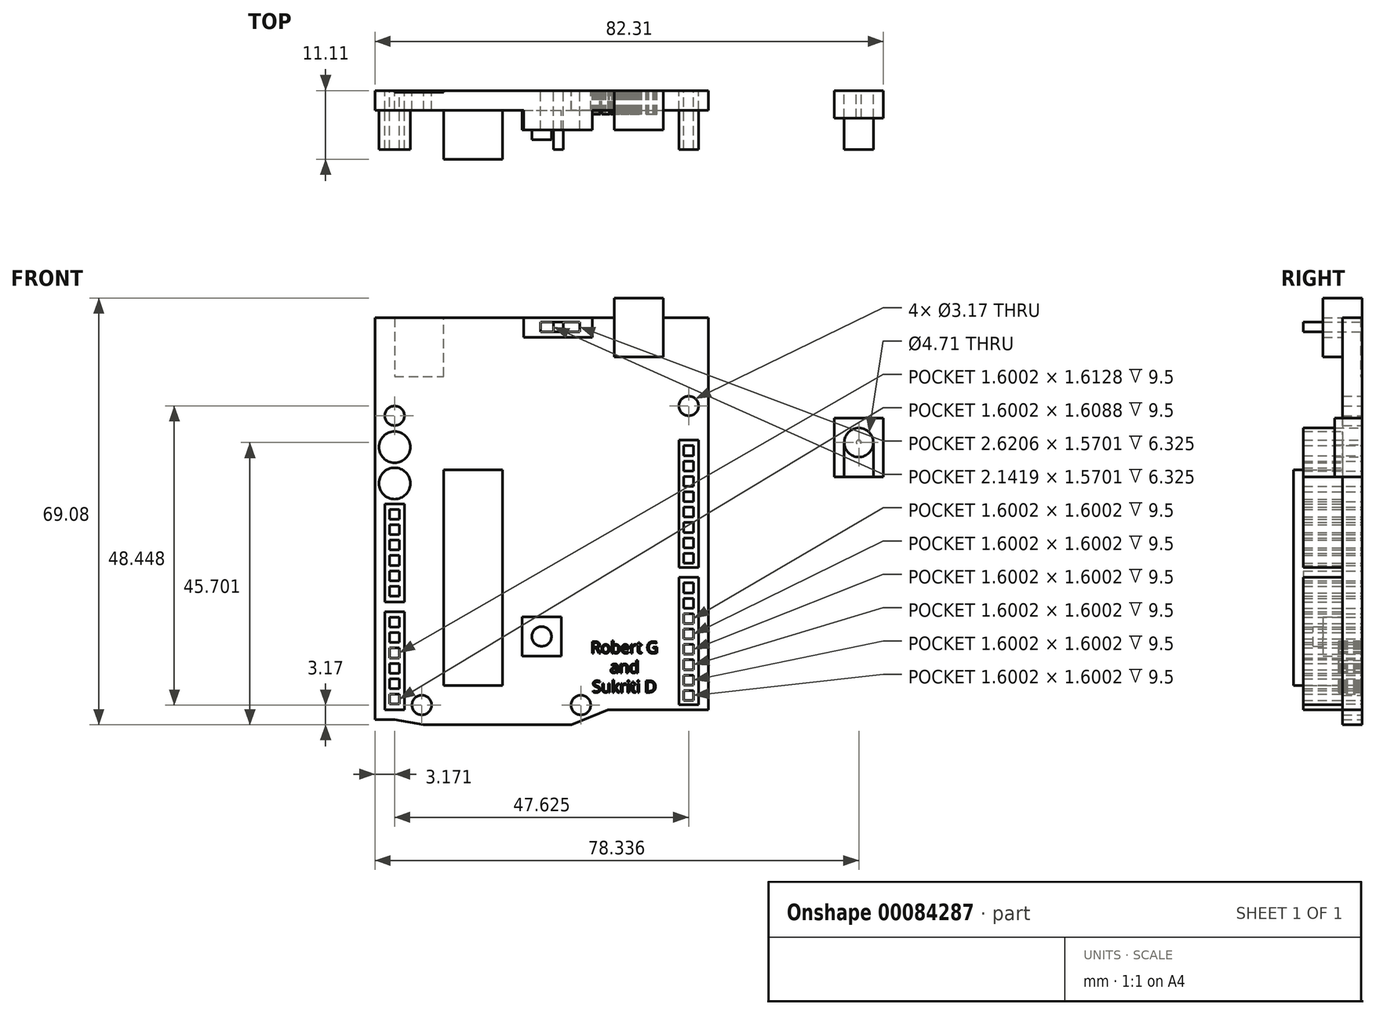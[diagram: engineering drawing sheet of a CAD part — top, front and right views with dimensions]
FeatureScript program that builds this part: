
annotation { "Feature Type Name" : "Feature", "Feature Type Description" : "" }
export const myFeature = defineFeature(function(context is Context, id is Id, definition is map)
    precondition{}
    {
        {
            var Q0;
            Q0=qCreatedBy(makeId("Front.planeOp"),FACE);
            var sketch = newSketch(context, id + "F0", { "sketchPlane" : qUnion([Q0])});
            skLineSegment(sketch, "E0.bottom", {"start": v(-35.3, 35.34) * mm, "end": v(18.68, 35.34) * mm});
            skLineSegment(sketch, "E0.top", {"start": v(-27.43, -30.57) * mm, "end": v(-3.44, -30.57) * mm});
            skLineSegment(sketch, "E0.left", {"start": v(-35.3, 35.34) * mm, "end": v(-35.3, -29.75) * mm});
            skLineSegment(sketch, "E0.right", {"start": v(18.68, 35.34) * mm, "end": v(18.68, -28.16) * mm});
            skLineSegment(sketch, "E1.bottom", {"start": v(-35.3, -29.75) * mm, "end": v(-32.12, -29.75) * mm});
            skPoint(sketch, "E2", {"position": v(-3.44, -30.57) * mm});
            skPoint(sketch, "E3.orphan", {"position": v(18.68, -30.57) * mm});
            skLineSegment(sketch, "E4", {"start": v(-32.12, -29.75) * mm, "end": v(-27.43, -30.57) * mm});
            skPoint(sketch, "E1.right.end.orphan", {"position": v(-35.19, -30.57) * mm});
            skLineSegment(sketch, "E5", {"start": v(-3.44, -30.57) * mm, "end": v(0.98, -28.76) * mm});
            skLineSegment(sketch, "E6", {"start": v(2.42, -28.16) * mm, "end": v(18.68, -28.16) * mm});
            skPoint(sketch, "E7.orphan", {"position": v(18.68, -30.95) * mm});
            skLineSegment(sketch, "E8", {"start": v(0.98, -28.76) * mm, "end": v(2.42, -28.16) * mm});
            skCircle(sketch, "E9", {"center": v(-27.72, -27.39) * mm, "radius": 1.59 * mm});
            skCircle(sketch, "E10", {"center": v(-1.96, -27.4) * mm, "radius": 1.59 * mm});
            skCircle(sketch, "E11", {"center": v(-32.12, 19.46) * mm, "radius": 1.59 * mm});
            skCircle(sketch, "E12", {"center": v(15.5, 21.05) * mm, "radius": 1.59 * mm});
            skLineSegment(sketch, "E13.bottom", {"start": v(11.14, 38.51) * mm, "end": v(11.4, 38.51) * mm});
            skLineSegment(sketch, "E13.top", {"start": v(3.47, 28.99) * mm, "end": v(11.4, 28.99) * mm});
            skLineSegment(sketch, "E14.bottom", {"start": v(13.92, -6.73) * mm, "end": v(17.1, -6.73) * mm});
            skLineSegment(sketch, "E14.top", {"start": v(13.92, -27.37) * mm, "end": v(17.1, -27.37) * mm});
            skLineSegment(sketch, "E14.left", {"start": v(13.92, -6.73) * mm, "end": v(13.92, -27.37) * mm});
            skLineSegment(sketch, "E14.right", {"start": v(17.1, -6.73) * mm, "end": v(17.1, -27.37) * mm});
            skLineSegment(sketch, "E15.bottom", {"start": v(13.92, 15.5) * mm, "end": v(17.1, 15.5) * mm});
            skLineSegment(sketch, "E15.top", {"start": v(13.92, -5.14) * mm, "end": v(17.1, -5.14) * mm});
            skLineSegment(sketch, "E15.left", {"start": v(13.92, 15.5) * mm, "end": v(13.92, -5.14) * mm});
            skLineSegment(sketch, "E15.right", {"start": v(17.1, 15.5) * mm, "end": v(17.1, -5.14) * mm});
            skLineSegment(sketch, "E16.bottom", {"start": v(-33.7, -12.29) * mm, "end": v(-30.53, -12.29) * mm});
            skLineSegment(sketch, "E16.top", {"start": v(-33.7, -28.16) * mm, "end": v(-30.53, -28.16) * mm});
            skLineSegment(sketch, "E16.left", {"start": v(-33.7, -12.29) * mm, "end": v(-33.7, -28.16) * mm});
            skLineSegment(sketch, "E16.right", {"start": v(-30.53, -12.29) * mm, "end": v(-30.53, -28.16) * mm});
            skLineSegment(sketch, "E17", {"start": v(-3.44, -30.57) * mm, "end": v(2.42, -28.16) * mm});
            skLineSegment(sketch, "E18.bottom", {"start": v(-33.7, 5.17) * mm, "end": v(-30.53, 5.17) * mm});
            skLineSegment(sketch, "E18.top", {"start": v(-33.7, -10.7) * mm, "end": v(-30.53, -10.7) * mm});
            skLineSegment(sketch, "E18.left", {"start": v(-33.7, 5.17) * mm, "end": v(-33.7, -10.7) * mm});
            skLineSegment(sketch, "E18.right", {"start": v(-30.53, 5.17) * mm, "end": v(-30.53, -10.7) * mm});
            skLineSegment(sketch, "E19.bottom", {"start": v(-24.18, -24.22) * mm, "end": v(-14.66, -24.22) * mm});
            skLineSegment(sketch, "E19.top", {"start": v(-24.18, 10.7) * mm, "end": v(-14.66, 10.7) * mm});
            skLineSegment(sketch, "E19.left", {"start": v(-24.18, -24.22) * mm, "end": v(-24.18, 10.7) * mm});
            skLineSegment(sketch, "E19.right", {"start": v(-14.66, -24.22) * mm, "end": v(-14.66, 10.7) * mm});
            skLineSegment(sketch, "E20.bottom", {"start": v(-11.48, -13.11) * mm, "end": v(-5.13, -13.11) * mm});
            skLineSegment(sketch, "E20.top", {"start": v(-11.48, -19.46) * mm, "end": v(-5.13, -19.46) * mm});
            skLineSegment(sketch, "E20.left", {"start": v(-11.48, -13.11) * mm, "end": v(-11.48, -19.46) * mm});
            skLineSegment(sketch, "E20.right", {"start": v(-5.13, -13.11) * mm, "end": v(-5.13, -19.46) * mm});
            skCircle(sketch, "E21", {"center": v(-8.3, -16.29) * mm, "radius": 1.59 * mm});
            skLineSegment(sketch, "E22.bottom", {"start": v(-11.2, 32.16) * mm, "end": v(-0.08, 32.16) * mm});
            skLineSegment(sketch, "E22.top", {"start": v(-11.2, 35.34) * mm, "end": v(-0.08, 35.34) * mm});
            skLineSegment(sketch, "E22.left", {"start": v(-11.2, 32.16) * mm, "end": v(-11.2, 35.34) * mm});
            skLineSegment(sketch, "E22.right", {"start": v(-0.08, 32.16) * mm, "end": v(-0.08, 35.34) * mm});
            skLineSegment(sketch, "E23.bottom", {"start": v(-8.5, 33.07) * mm, "end": v(-2.16, 33.07) * mm});
            skLineSegment(sketch, "E23.top", {"start": v(-8.5, 34.64) * mm, "end": v(-2.16, 34.64) * mm});
            skLineSegment(sketch, "E23.left", {"start": v(-8.5, 33.07) * mm, "end": v(-8.5, 34.64) * mm});
            skLineSegment(sketch, "E24", {"start": v(-2.16, 34.64) * mm, "end": v(-2.16, 33.07) * mm});
            skLineSegment(sketch, "E25", {"start": v(-4.78, 34.64) * mm, "end": v(-4.78, 33.07) * mm});
            skLineSegment(sketch, "E26", {"start": v(-6.37, 34.64) * mm, "end": v(-6.37, 33.07) * mm});
            skLineSegment(sketch, "E27", {"start": v(11.4, 36.51) * mm, "end": v(11.4, 35.34) * mm});
            skLineSegment(sketch, "E28.trimOffspring", {"start": v(3.47, 35.34) * mm, "end": v(3.47, 28.99) * mm});
            skLineSegment(sketch, "E29.trimOffspring", {"start": v(11.4, 35.34) * mm, "end": v(11.4, 28.99) * mm});
            skPoint(sketch, "E30.orphan", {"position": v(3.47, 38.51) * mm});
            skLineSegment(sketch, "E31", {"start": v(3.47, 35.34) * mm, "end": v(3.47, 36.51) * mm});
            skLineSegment(sketch, "E32", {"start": v(11.14, 38.51) * mm, "end": v(3.73, 38.51) * mm});
            skLineSegment(sketch, "E33", {"start": v(-32.12, 35.34) * mm, "end": v(-32.12, 25.81) * mm});
            skLineSegment(sketch, "E34", {"start": v(-32.12, 25.81) * mm, "end": v(-24.17, 25.81) * mm});
            skLineSegment(sketch, "E35", {"start": v(-24.17, 25.81) * mm, "end": v(-24.17, 35.34) * mm});
            skLineSegment(sketch, "E36.bottom", {"start": v(-32.9, 4.28) * mm, "end": v(-31.32, 4.28) * mm});
            skLineSegment(sketch, "E36.top", {"start": v(-32.9, 2.7) * mm, "end": v(-31.32, 2.7) * mm});
            skLineSegment(sketch, "E36.left", {"start": v(-32.9, 4.28) * mm, "end": v(-32.9, 2.7) * mm});
            skLineSegment(sketch, "E36.right", {"start": v(-31.32, 4.28) * mm, "end": v(-31.32, 2.7) * mm});
            skLineSegment(sketch, "E37.left", {"start": v(-32.9, 1.25) * mm, "end": v(-32.9, 1.22) * mm});
            skLineSegment(sketch, "E37.right", {"start": v(-31.53, 1.25) * mm, "end": v(-31.53, 1.22) * mm});
            skLineSegment(sketch, "E38.bottom", {"start": v(-32.9, 1.8) * mm, "end": v(-31.32, 1.8) * mm});
            skLineSegment(sketch, "E38.top", {"start": v(-32.9, 0.2) * mm, "end": v(-31.32, 0.2) * mm});
            skLineSegment(sketch, "E38.left", {"start": v(-32.9, 1.8) * mm, "end": v(-32.9, 0.2) * mm});
            skLineSegment(sketch, "E38.right", {"start": v(-31.32, 1.8) * mm, "end": v(-31.32, 0.2) * mm});
            skLineSegment(sketch, "E39.bottom", {"start": v(-32.9, -0.68) * mm, "end": v(-31.32, -0.68) * mm});
            skLineSegment(sketch, "E39.top", {"start": v(-32.9, -2.28) * mm, "end": v(-31.32, -2.28) * mm});
            skLineSegment(sketch, "E39.left", {"start": v(-32.9, -0.68) * mm, "end": v(-32.9, -2.28) * mm});
            skLineSegment(sketch, "E39.right", {"start": v(-31.32, -0.68) * mm, "end": v(-31.32, -2.28) * mm});
            skLineSegment(sketch, "E40.bottom", {"start": v(-32.9, -3.17) * mm, "end": v(-31.32, -3.17) * mm});
            skLineSegment(sketch, "E40.top", {"start": v(-32.9, -4.77) * mm, "end": v(-31.32, -4.77) * mm});
            skLineSegment(sketch, "E40.left", {"start": v(-32.9, -3.17) * mm, "end": v(-32.9, -4.77) * mm});
            skLineSegment(sketch, "E40.right", {"start": v(-31.32, -3.17) * mm, "end": v(-31.32, -4.77) * mm});
            skLineSegment(sketch, "E41.bottom", {"start": v(-32.9, -5.66) * mm, "end": v(-31.32, -5.66) * mm});
            skLineSegment(sketch, "E41.top", {"start": v(-32.9, -7.26) * mm, "end": v(-31.32, -7.26) * mm});
            skLineSegment(sketch, "E41.left", {"start": v(-32.9, -5.66) * mm, "end": v(-32.9, -7.26) * mm});
            skLineSegment(sketch, "E41.right", {"start": v(-31.32, -5.66) * mm, "end": v(-31.32, -7.26) * mm});
            skLineSegment(sketch, "E42.bottom", {"start": v(-32.9, -8.15) * mm, "end": v(-31.32, -8.15) * mm});
            skLineSegment(sketch, "E42.top", {"start": v(-32.9, -9.75) * mm, "end": v(-31.32, -9.75) * mm});
            skLineSegment(sketch, "E42.left", {"start": v(-32.9, -8.15) * mm, "end": v(-32.9, -9.75) * mm});
            skLineSegment(sketch, "E42.right", {"start": v(-31.32, -8.15) * mm, "end": v(-31.32, -9.75) * mm});
            skLineSegment(sketch, "E43.bottom", {"start": v(-32.92, -13.18) * mm, "end": v(-31.32, -13.18) * mm});
            skLineSegment(sketch, "E43.top", {"start": v(-32.92, -14.78) * mm, "end": v(-31.32, -14.78) * mm});
            skLineSegment(sketch, "E43.left", {"start": v(-32.92, -13.18) * mm, "end": v(-32.92, -14.78) * mm});
            skLineSegment(sketch, "E43.right", {"start": v(-31.32, -13.18) * mm, "end": v(-31.32, -14.78) * mm});
            skLineSegment(sketch, "E44.bottom", {"start": v(-32.92, -15.67) * mm, "end": v(-31.32, -15.67) * mm});
            skLineSegment(sketch, "E44.top", {"start": v(-32.92, -17.27) * mm, "end": v(-31.32, -17.27) * mm});
            skLineSegment(sketch, "E44.left", {"start": v(-32.92, -15.67) * mm, "end": v(-32.92, -17.27) * mm});
            skLineSegment(sketch, "E44.right", {"start": v(-31.32, -15.67) * mm, "end": v(-31.32, -17.27) * mm});
            skLineSegment(sketch, "E45.bottom", {"start": v(-32.92, -18.16) * mm, "end": v(-31.32, -18.16) * mm});
            skLineSegment(sketch, "E45.top", {"start": v(-32.92, -19.77) * mm, "end": v(-31.32, -19.77) * mm});
            skLineSegment(sketch, "E45.left", {"start": v(-32.92, -18.16) * mm, "end": v(-32.92, -19.77) * mm});
            skLineSegment(sketch, "E45.right", {"start": v(-31.32, -18.16) * mm, "end": v(-31.32, -19.77) * mm});
            skLineSegment(sketch, "E46.bottom", {"start": v(-32.92, -20.66) * mm, "end": v(-31.32, -20.66) * mm});
            skLineSegment(sketch, "E46.top", {"start": v(-32.92, -22.26) * mm, "end": v(-31.32, -22.26) * mm});
            skLineSegment(sketch, "E46.left", {"start": v(-32.92, -20.66) * mm, "end": v(-32.92, -22.26) * mm});
            skLineSegment(sketch, "E46.right", {"start": v(-31.32, -20.66) * mm, "end": v(-31.32, -22.26) * mm});
            skLineSegment(sketch, "E47.bottom", {"start": v(-32.92, -23.15) * mm, "end": v(-31.32, -23.15) * mm});
            skLineSegment(sketch, "E47.top", {"start": v(-32.92, -24.74) * mm, "end": v(-31.32, -24.74) * mm});
            skLineSegment(sketch, "E47.left", {"start": v(-32.92, -23.15) * mm, "end": v(-32.92, -24.74) * mm});
            skLineSegment(sketch, "E47.right", {"start": v(-31.32, -23.15) * mm, "end": v(-31.32, -24.74) * mm});
            skLineSegment(sketch, "E48.bottom", {"start": v(-32.92, -25.62) * mm, "end": v(-31.32, -25.62) * mm});
            skLineSegment(sketch, "E48.top", {"start": v(-32.92, -27.23) * mm, "end": v(-31.32, -27.23) * mm});
            skLineSegment(sketch, "E48.left", {"start": v(-32.92, -25.62) * mm, "end": v(-32.92, -27.23) * mm});
            skLineSegment(sketch, "E48.right", {"start": v(-31.32, -25.62) * mm, "end": v(-31.32, -27.23) * mm});
            skLineSegment(sketch, "E49.bottom", {"start": v(14.7, 14.6) * mm, "end": v(16.3, 14.6) * mm});
            skLineSegment(sketch, "E49.top", {"start": v(14.7, 13) * mm, "end": v(16.3, 13) * mm});
            skLineSegment(sketch, "E49.left", {"start": v(14.7, 14.6) * mm, "end": v(14.7, 13) * mm});
            skLineSegment(sketch, "E49.right", {"start": v(16.3, 14.6) * mm, "end": v(16.3, 13) * mm});
            skLineSegment(sketch, "E50.bottom", {"start": v(14.7, 12.12) * mm, "end": v(16.3, 12.12) * mm});
            skLineSegment(sketch, "E50.top", {"start": v(14.7, 10.52) * mm, "end": v(16.3, 10.52) * mm});
            skLineSegment(sketch, "E50.left", {"start": v(14.7, 12.12) * mm, "end": v(14.7, 10.52) * mm});
            skLineSegment(sketch, "E50.right", {"start": v(16.3, 12.12) * mm, "end": v(16.3, 10.52) * mm});
            skLineSegment(sketch, "E51.bottom", {"start": v(14.7, 9.63) * mm, "end": v(16.3, 9.63) * mm});
            skLineSegment(sketch, "E51.top", {"start": v(14.7, 8.03) * mm, "end": v(16.3, 8.03) * mm});
            skLineSegment(sketch, "E51.left", {"start": v(14.7, 9.63) * mm, "end": v(14.7, 8.03) * mm});
            skLineSegment(sketch, "E51.right", {"start": v(16.3, 9.63) * mm, "end": v(16.3, 8.03) * mm});
            skLineSegment(sketch, "E52.bottom", {"start": v(14.7, 7.14) * mm, "end": v(16.3, 7.14) * mm});
            skLineSegment(sketch, "E52.top", {"start": v(14.7, 5.54) * mm, "end": v(16.3, 5.54) * mm});
            skLineSegment(sketch, "E52.left", {"start": v(14.7, 7.14) * mm, "end": v(14.7, 5.54) * mm});
            skLineSegment(sketch, "E52.right", {"start": v(16.3, 7.14) * mm, "end": v(16.3, 5.54) * mm});
            skLineSegment(sketch, "E53.bottom", {"start": v(14.7, 4.65) * mm, "end": v(16.3, 4.65) * mm});
            skLineSegment(sketch, "E53.top", {"start": v(14.7, 3.05) * mm, "end": v(16.3, 3.05) * mm});
            skLineSegment(sketch, "E53.left", {"start": v(14.7, 4.65) * mm, "end": v(14.7, 3.05) * mm});
            skLineSegment(sketch, "E53.right", {"start": v(16.3, 4.65) * mm, "end": v(16.3, 3.05) * mm});
            skLineSegment(sketch, "E54.bottom", {"start": v(14.7, 2.16) * mm, "end": v(16.3, 2.16) * mm});
            skLineSegment(sketch, "E54.top", {"start": v(14.7, 0.56) * mm, "end": v(16.3, 0.56) * mm});
            skLineSegment(sketch, "E54.left", {"start": v(14.7, 2.16) * mm, "end": v(14.7, 0.56) * mm});
            skLineSegment(sketch, "E54.right", {"start": v(16.3, 2.16) * mm, "end": v(16.3, 0.56) * mm});
            skLineSegment(sketch, "E55.bottom", {"start": v(14.7, -0.33) * mm, "end": v(16.3, -0.33) * mm});
            skLineSegment(sketch, "E55.top", {"start": v(14.7, -1.92) * mm, "end": v(16.3, -1.92) * mm});
            skLineSegment(sketch, "E55.left", {"start": v(14.7, -0.33) * mm, "end": v(14.7, -1.92) * mm});
            skLineSegment(sketch, "E55.right", {"start": v(16.3, -0.33) * mm, "end": v(16.3, -1.92) * mm});
            skLineSegment(sketch, "E56.bottom", {"start": v(14.7, -2.8) * mm, "end": v(16.3, -2.8) * mm});
            skLineSegment(sketch, "E56.top", {"start": v(14.7, -4.4) * mm, "end": v(16.3, -4.4) * mm});
            skLineSegment(sketch, "E56.left", {"start": v(14.7, -2.8) * mm, "end": v(14.7, -4.4) * mm});
            skLineSegment(sketch, "E56.right", {"start": v(16.3, -2.8) * mm, "end": v(16.3, -4.4) * mm});
            skLineSegment(sketch, "E57.bottom", {"start": v(14.7, -7.62) * mm, "end": v(16.3, -7.62) * mm});
            skLineSegment(sketch, "E57.top", {"start": v(14.7, -9.22) * mm, "end": v(16.3, -9.22) * mm});
            skLineSegment(sketch, "E57.left", {"start": v(14.7, -7.62) * mm, "end": v(14.7, -9.22) * mm});
            skLineSegment(sketch, "E57.right", {"start": v(16.3, -7.62) * mm, "end": v(16.3, -9.22) * mm});
            skLineSegment(sketch, "E58.bottom", {"start": v(14.7, -10.1) * mm, "end": v(16.3, -10.1) * mm});
            skLineSegment(sketch, "E58.top", {"start": v(14.7, -11.7) * mm, "end": v(16.3, -11.7) * mm});
            skLineSegment(sketch, "E58.left", {"start": v(14.7, -10.1) * mm, "end": v(14.7, -11.7) * mm});
            skLineSegment(sketch, "E58.right", {"start": v(16.3, -10.1) * mm, "end": v(16.3, -11.7) * mm});
            skLineSegment(sketch, "E59.bottom", {"start": v(14.7, -12.6) * mm, "end": v(16.3, -12.6) * mm});
            skLineSegment(sketch, "E59.top", {"start": v(14.7, -14.2) * mm, "end": v(16.3, -14.2) * mm});
            skLineSegment(sketch, "E59.left", {"start": v(14.7, -12.6) * mm, "end": v(14.7, -14.2) * mm});
            skLineSegment(sketch, "E59.right", {"start": v(16.3, -12.6) * mm, "end": v(16.3, -14.2) * mm});
            skLineSegment(sketch, "E60.bottom", {"start": v(14.7, -15.09) * mm, "end": v(16.3, -15.09) * mm});
            skLineSegment(sketch, "E60.top", {"start": v(14.7, -16.69) * mm, "end": v(16.3, -16.69) * mm});
            skLineSegment(sketch, "E60.left", {"start": v(14.7, -15.09) * mm, "end": v(14.7, -16.69) * mm});
            skLineSegment(sketch, "E60.right", {"start": v(16.3, -15.09) * mm, "end": v(16.3, -16.69) * mm});
            skLineSegment(sketch, "E61.bottom", {"start": v(14.7, -17.58) * mm, "end": v(16.3, -17.58) * mm});
            skLineSegment(sketch, "E61.top", {"start": v(14.7, -19.18) * mm, "end": v(16.3, -19.18) * mm});
            skLineSegment(sketch, "E61.left", {"start": v(14.7, -17.58) * mm, "end": v(14.7, -19.18) * mm});
            skLineSegment(sketch, "E61.right", {"start": v(16.3, -17.58) * mm, "end": v(16.3, -19.18) * mm});
            skLineSegment(sketch, "E62.bottom", {"start": v(14.7, -20.07) * mm, "end": v(16.3, -20.07) * mm});
            skLineSegment(sketch, "E62.top", {"start": v(14.7, -21.67) * mm, "end": v(16.3, -21.67) * mm});
            skLineSegment(sketch, "E62.left", {"start": v(14.7, -20.07) * mm, "end": v(14.7, -21.67) * mm});
            skLineSegment(sketch, "E62.right", {"start": v(16.3, -20.07) * mm, "end": v(16.3, -21.67) * mm});
            skLineSegment(sketch, "E63.bottom", {"start": v(14.7, -22.56) * mm, "end": v(16.3, -22.56) * mm});
            skLineSegment(sketch, "E63.top", {"start": v(14.7, -24.16) * mm, "end": v(16.3, -24.16) * mm});
            skLineSegment(sketch, "E63.left", {"start": v(14.7, -22.56) * mm, "end": v(14.7, -24.16) * mm});
            skLineSegment(sketch, "E63.right", {"start": v(16.3, -22.56) * mm, "end": v(16.3, -24.16) * mm});
            skLineSegment(sketch, "E64.bottom", {"start": v(14.7, -25.04) * mm, "end": v(16.3, -25.04) * mm});
            skLineSegment(sketch, "E64.top", {"start": v(14.7, -26.64) * mm, "end": v(16.3, -26.64) * mm});
            skLineSegment(sketch, "E64.left", {"start": v(14.7, -25.04) * mm, "end": v(14.7, -26.64) * mm});
            skLineSegment(sketch, "E64.right", {"start": v(16.3, -25.04) * mm, "end": v(16.3, -26.64) * mm});
            skPoint(sketch, "E65.end.orphan", {"position": v(3.73, 37.04) * mm});
            skPoint(sketch, "E66.end.orphan", {"position": v(11.14, 37.04) * mm});
            skLineSegment(sketch, "E67", {"start": v(11.4, 36.51) * mm, "end": v(11.4, 38.51) * mm});
            skLineSegment(sketch, "E68", {"start": v(3.47, 36.51) * mm, "end": v(3.47, 38.51) * mm});
            skLineSegment(sketch, "E69", {"start": v(3.47, 38.51) * mm, "end": v(3.73, 38.51) * mm});
            skCircle(sketch, "E70", {"center": v(-32.12, 8.5) * mm, "radius": 2.54 * mm});
            skCircle(sketch, "E71", {"center": v(-32.12, 14.38) * mm, "radius": 2.54 * mm});
            skPoint(sketch, "E72.left.end.orphan", {"position": v(13.92, 17.84) * mm});
            skPoint(sketch, "E72.bottom.start.orphan", {"position": v(13.92, 16.26) * mm});
            skPoint(sketch, "E72.right.end.orphan", {"position": v(17.1, 17.84) * mm});
            skSolve(sketch);
        }
        {
            var Q0;
            Q0=qCreatedBy(makeId("Front.planeOp"),FACE);
            var sketch = newSketch(context, id + "F1", { "sketchPlane" : qUnion([Q0])});
            skLineSegment(sketch, "E73.bottom", {"start": v(39.08, 19.07) * mm, "end": v(47.02, 19.07) * mm});
            skLineSegment(sketch, "E73.top", {"start": v(39.08, 9.55) * mm, "end": v(47.02, 9.55) * mm});
            skLineSegment(sketch, "E73.left", {"start": v(39.08, 19.07) * mm, "end": v(39.08, 9.55) * mm});
            skLineSegment(sketch, "E73.right", {"start": v(47.02, 19.07) * mm, "end": v(47.02, 9.55) * mm});
            skLineSegment(sketch, "E74", {"start": v(43.05, 12.83) * mm, "end": v(43.05, 12.72) * mm});
            skLineSegment(sketch, "E75", {"start": v(43.05, 12.83) * mm, "end": v(43.05, 12.78) * mm});
            skPoint(sketch, "E76.orphan", {"position": v(43.05, 9.55) * mm});
            skPoint(sketch, "E77", {"position": v(43.05, 17.49) * mm});
            skPoint(sketch, "E78.orphan", {"position": v(43.05, 19.07) * mm});
            skArc(sketch, "E79", {"start": v(43, 12.78) * mm, "mid": v(43.05, 12.78) * mm, "end": v(43.1, 12.78) * mm});
            skCircle(sketch, "E80", {"center": v(43.05, 15.13) * mm, "radius": 0.8 * mm});
            skLineSegment(sketch, "E81", {"start": v(40.7, 15.13) * mm, "end": v(40.7, 9.55) * mm});
            skLineSegment(sketch, "E82", {"start": v(45.4, 15.13) * mm, "end": v(45.4, 9.55) * mm});
            skArc(sketch, "E83.trimOffspring", {"start": v(45.4, 15.13) * mm, "mid": v(43.05, 17.49) * mm, "end": v(40.7, 15.13) * mm});
            skCircle(sketch, "E84", {"center": v(43.05, 15.13) * mm, "radius": 0.4 * mm});
            skArc(sketch, "E85", {"start": v(40.7, 15.13) * mm, "mid": v(43.05, 12.78) * mm, "end": v(45.4, 15.13) * mm});
            skSolve(sketch);
        }
        {
            var Q0;
            {var subQ7=sQuery(id+"F0.wireOp",EDGE,"E0.left");Q0=makeQuery(id+"F0.imprint","IMPRINT",FACE,{"disambiguationData":[TD([[makeQuery(id+"F0.imprint","IMPRINT",EDGE,{"derivedFrom":subQ7}),1.0]])]});}
            var Q1;
            {var subQ0=sQuery(id+"F0.wireOp",EDGE,"E33");Q1=makeQuery(id+"F0.imprint","IMPRINT",FACE,{"disambiguationData":[TD([[makeQuery(id+"F0.imprint","IMPRINT",EDGE,{"derivedFrom":subQ0}),1.0]])]});}
            extrude(context, id + "F2", {"entities" : qUnion([Q0, Q1]), "depth" : 3.17 * mm});
        }
        {
            var Q0;
            Q0=makeQuery(id+"F0.imprint","IMPRINT",FACE,{"disambiguationData":[TD([[makeQuery(id+"F0.imprint","IMPRINT",EDGE,{"derivedFrom":sQuery(id+"F0.wireOp",EDGE,"E22.bottom")}),1.0]])]});
            extrude(context, id + "F3", {"entities" : qUnion([Q0]), "operationType" : NewBodyOperationType.ADD, "depth" : 6.35 * mm});
        }
        {
            var Q0;
            {var subQ0=sQuery(id+"F0.wireOp",EDGE,"E25");Q0=makeQuery(id+"F0.imprint","IMPRINT",FACE,{"disambiguationData":[TD([[makeQuery(id+"F0.imprint","IMPRINT",EDGE,{"derivedFrom":subQ0}),-1.0]])]});}
            extrude(context, id + "F4", {"entities" : qUnion([Q0]), "operationType" : NewBodyOperationType.ADD, "depth" : 9.52 * mm});
        }
        {
            var Q0;
            Q0=makeQuery(id+"F0.imprint","IMPRINT",FACE,{"disambiguationData":[TD([[makeQuery(id+"F0.imprint","IMPRINT",EDGE,{"derivedFrom":sQuery(id+"F0.wireOp",EDGE,"E14.bottom")}),-1.0]])]});
            var Q1;
            Q1=makeQuery(id+"F0.imprint","IMPRINT",FACE,{"disambiguationData":[TD([[makeQuery(id+"F0.imprint","IMPRINT",EDGE,{"derivedFrom":sQuery(id+"F0.wireOp",EDGE,"E15.bottom")}),-1.0]])]});
            var Q2;
            Q2=makeQuery(id+"F0.imprint","IMPRINT",FACE,{"disambiguationData":[TD([[makeQuery(id+"F0.imprint","IMPRINT",EDGE,{"derivedFrom":sQuery(id+"F0.wireOp",EDGE,"E18.bottom")}),-1.0]])]});
            var Q3;
            Q3=makeQuery(id+"F0.imprint","IMPRINT",FACE,{"disambiguationData":[TD([[makeQuery(id+"F0.imprint","IMPRINT",EDGE,{"derivedFrom":sQuery(id+"F0.wireOp",EDGE,"E16.bottom")}),-1.0]])]});
            extrude(context, id + "F5", {"entities" : qUnion([Q0, Q1, Q2, Q3]), "operationType" : NewBodyOperationType.ADD, "depth" : 9.52 * mm});
        }
        {
            var Q0;
            Q0=makeQuery(id+"F0.imprint","IMPRINT",FACE,{"disambiguationData":[TD([[makeQuery(id+"F0.imprint","IMPRINT",EDGE,{"derivedFrom":sQuery(id+"F0.wireOp",EDGE,"E19.bottom")}),1.0]])]});
            extrude(context, id + "F6", {"entities" : qUnion([Q0]), "operationType" : NewBodyOperationType.ADD, "depth" : 11.1 * mm});
        }
        {
            var Q0;
            {var subQ0=sQuery(id+"F0.wireOp",EDGE,"E27");Q0=makeQuery(id+"F0.imprint","IMPRINT",FACE,{"disambiguationData":[TD([[makeQuery(id+"F0.imprint","IMPRINT",EDGE,{"derivedFrom":subQ0}),-1.0]])]});}
            var Q1;
            Q1=makeQuery(id+"F0.imprint","IMPRINT",FACE,{"disambiguationData":[TD([[makeQuery(id+"F0.imprint","IMPRINT",EDGE,{"derivedFrom":sQuery(id+"F0.wireOp",EDGE,"E13.top")}),1.0]])]});
            extrude(context, id + "F7", {"entities" : qUnion([Q0, Q1]), "operationType" : NewBodyOperationType.ADD, "depth" : 6.35 * mm});
        }
        {
            var Q0;
            Q0=makeQuery(id+"F0.imprint","IMPRINT",FACE,{"disambiguationData":[TD([[makeQuery(id+"F0.imprint","IMPRINT",EDGE,{"derivedFrom":sQuery(id+"F0.wireOp",EDGE,"E20.bottom")}),-1.0]])]});
            extrude(context, id + "F8", {"entities" : qUnion([Q0]), "operationType" : NewBodyOperationType.ADD, "depth" : 6.35 * mm});
        }
        {
            var Q0;
            Q0=makeQuery(id+"F0.imprint","IMPRINT",FACE,{"disambiguationData":[TD([[makeQuery(id+"F0.imprint","IMPRINT",EDGE,{"derivedFrom":sQuery(id+"F0.wireOp",EDGE,"E21")}),1.0]])]});
            extrude(context, id + "F9", {"entities" : qUnion([Q0]), "operationType" : NewBodyOperationType.ADD, "depth" : 7.94 * mm});
        }
        {
            var Q0;
            Q0=qCreatedBy(makeId("Front.planeOp"),FACE);
            var sketch = newSketch(context, id + "F10", { "sketchPlane" : qUnion([Q0])});
            skText(sketch, "E86", { "text": "Robert G", "fontName": "OpenSans-Regular.ttf"});
            skText(sketch, "E87", { "text": "and", "fontName": "OpenSans-Regular.ttf"});
            skText(sketch, "E88", { "text": "Sukriti D", "fontName": "OpenSans-Regular.ttf"});
            skLineSegment(sketch, "E89", {"start": v(5.01, -19.27) * mm, "end": v(5.01, -20.54) * mm, "construction": true});
            skLineSegment(sketch, "E90", {"start": v(5.01, -22.45) * mm, "end": v(5.01, -23.72) * mm, "construction": true});
            const initialGuessF10  = {"E86": [-0.00037, -0.019, 1, 0, 0.0019], "E87": [0.00277, -0.02217, 1, 0, 0.0019], "E88": [-0.00012, -0.02534, 1, 0, 0.0019]};
            skSetInitialGuess(sketch, initialGuessF10);
            skSolve(sketch);
        }
        {
            var Q0;
            {var subQ0=sQuery(id+"F0.wireOp",EDGE,"E33");Q0=makeQuery(id+"F0.imprint","IMPRINT",FACE,{"disambiguationData":[TD([[makeQuery(id+"F0.imprint","IMPRINT",EDGE,{"derivedFrom":subQ0}),1.0]])]});}
            extrude(context, id + "F11", {"entities" : qUnion([Q0]), "depth" : 0.25 * mm});
        }
        {
            var Q0;
            Q0 = qSketchRegion(id + "F10", true);
            extrude(context, id + "F12", {"entities" : qUnion([Q0]), "depth" : 3.8 * mm});
        }
        {
            var Q0;
            Q0=makeQuery(id+"F1.imprint","IMPRINT",FACE,{"disambiguationData":[TD([[makeQuery(id+"F1.imprint","IMPRINT",EDGE,{"derivedFrom":sQuery(id+"F1.wireOp",EDGE,"E73.bottom")}),-1.0]])]});
            var Q1;
            {var subQ2=sQuery(id+"F1.wireOp",EDGE,"E81");Q1=makeQuery(id+"F1.imprint","IMPRINT",FACE,{"disambiguationData":[TD([[makeQuery(id+"F1.imprint","IMPRINT",EDGE,{"derivedFrom":subQ2}),1.0]])]});}
            var Q2;
            Q2=makeQuery(id+"F1.imprint","IMPRINT",FACE,{"disambiguationData":[TD([[makeQuery(id+"F1.imprint","IMPRINT",EDGE,{"derivedFrom":sQuery(id+"F1.wireOp",EDGE,"E84")}),1.0]])]});
            extrude(context, id + "F13", {"entities" : qUnion([Q0, Q1, Q2]), "depth" : 4.44 * mm});
        }
        {
            var Q0;
            Q0=makeQuery(id+"F1.imprint","IMPRINT",FACE,{"disambiguationData":[TD([[makeQuery(id+"F1.imprint","IMPRINT",EDGE,{"derivedFrom":sQuery(id+"F1.wireOp",EDGE,"E80")}),-1.0]])]});
            var Q1;
            {var subQ2=sQuery(id+"F1.wireOp",EDGE,"E81");Q1=makeQuery(id+"F1.imprint","IMPRINT",FACE,{"disambiguationData":[TD([[makeQuery(id+"F1.imprint","IMPRINT",EDGE,{"derivedFrom":subQ2}),1.0]])]});}
            var Q2;
            Q2=makeQuery(id+"F1.imprint","IMPRINT",FACE,{"disambiguationData":[TD([[makeQuery(id+"F1.imprint","IMPRINT",EDGE,{"derivedFrom":sQuery(id+"F1.wireOp",EDGE,"E80")}),1.0]])]});
            var Q3;
            Q3=makeQuery(id+"F1.imprint","IMPRINT",FACE,{"disambiguationData":[TD([[makeQuery(id+"F1.imprint","IMPRINT",EDGE,{"derivedFrom":sQuery(id+"F1.wireOp",EDGE,"E84")}),1.0]])]});
            extrude(context, id + "F14", {"entities" : qUnion([Q0, Q1, Q2, Q3]), "depth" : 9.52 * mm});
        }
        {
            var Q0;
            Q0=makeQuery(id+"F0.imprint","IMPRINT",FACE,{"disambiguationData":[TD([[makeQuery(id+"F0.imprint","IMPRINT",EDGE,{"derivedFrom":sQuery(id+"F0.wireOp",EDGE,"E39.bottom")}),-1.0]])]});
            var Q1;
            Q1=makeQuery(id+"F0.imprint","IMPRINT",FACE,{"disambiguationData":[TD([[makeQuery(id+"F0.imprint","IMPRINT",EDGE,{"derivedFrom":sQuery(id+"F0.wireOp",EDGE,"E38.bottom")}),-1.0]])]});
            var Q2;
            Q2=makeQuery(id+"F0.imprint","IMPRINT",FACE,{"disambiguationData":[TD([[makeQuery(id+"F0.imprint","IMPRINT",EDGE,{"derivedFrom":sQuery(id+"F0.wireOp",EDGE,"E36.bottom")}),-1.0]])]});
            var Q3;
            Q3=makeQuery(id+"F0.imprint","IMPRINT",FACE,{"disambiguationData":[TD([[makeQuery(id+"F0.imprint","IMPRINT",EDGE,{"derivedFrom":sQuery(id+"F0.wireOp",EDGE,"E40.bottom")}),-1.0]])]});
            var Q4;
            Q4=makeQuery(id+"F0.imprint","IMPRINT",FACE,{"disambiguationData":[TD([[makeQuery(id+"F0.imprint","IMPRINT",EDGE,{"derivedFrom":sQuery(id+"F0.wireOp",EDGE,"E42.bottom")}),-1.0]])]});
            var Q5;
            Q5=makeQuery(id+"F0.imprint","IMPRINT",FACE,{"disambiguationData":[TD([[makeQuery(id+"F0.imprint","IMPRINT",EDGE,{"derivedFrom":sQuery(id+"F0.wireOp",EDGE,"E41.bottom")}),-1.0]])]});
            extrude(context, id + "F15", {"entities" : qUnion([Q0, Q1, Q2, Q3, Q4, Q5]), "operationType" : NewBodyOperationType.ADD, "depth" : 0.03 * mm});
        }
        {
            var Q0;
            Q0=makeQuery(id+"F0.imprint","IMPRINT",FACE,{"disambiguationData":[TD([[makeQuery(id+"F0.imprint","IMPRINT",EDGE,{"derivedFrom":sQuery(id+"F0.wireOp",EDGE,"E43.bottom")}),-1.0]])]});
            var Q1;
            Q1=makeQuery(id+"F0.imprint","IMPRINT",FACE,{"disambiguationData":[TD([[makeQuery(id+"F0.imprint","IMPRINT",EDGE,{"derivedFrom":sQuery(id+"F0.wireOp",EDGE,"E44.bottom")}),-1.0]])]});
            var Q2;
            Q2=makeQuery(id+"F0.imprint","IMPRINT",FACE,{"disambiguationData":[TD([[makeQuery(id+"F0.imprint","IMPRINT",EDGE,{"derivedFrom":sQuery(id+"F0.wireOp",EDGE,"E45.bottom")}),-1.0]])]});
            var Q3;
            Q3=makeQuery(id+"F0.imprint","IMPRINT",FACE,{"disambiguationData":[TD([[makeQuery(id+"F0.imprint","IMPRINT",EDGE,{"derivedFrom":sQuery(id+"F0.wireOp",EDGE,"E46.bottom")}),-1.0]])]});
            var Q4;
            Q4=makeQuery(id+"F0.imprint","IMPRINT",FACE,{"disambiguationData":[TD([[makeQuery(id+"F0.imprint","IMPRINT",EDGE,{"derivedFrom":sQuery(id+"F0.wireOp",EDGE,"E47.bottom")}),-1.0]])]});
            var Q5;
            Q5=makeQuery(id+"F0.imprint","IMPRINT",FACE,{"disambiguationData":[TD([[makeQuery(id+"F0.imprint","IMPRINT",EDGE,{"derivedFrom":sQuery(id+"F0.wireOp",EDGE,"E48.bottom")}),-1.0]])]});
            extrude(context, id + "F16", {"entities" : qUnion([Q0, Q1, Q2, Q3, Q4, Q5]), "operationType" : NewBodyOperationType.ADD, "depth" : 0.03 * mm});
        }
        {
            var Q0;
            Q0=makeQuery(id+"F0.imprint","IMPRINT",FACE,{"disambiguationData":[TD([[makeQuery(id+"F0.imprint","IMPRINT",EDGE,{"derivedFrom":sQuery(id+"F0.wireOp",EDGE,"E49.bottom")}),-1.0]])]});
            var Q1;
            Q1=makeQuery(id+"F0.imprint","IMPRINT",FACE,{"disambiguationData":[TD([[makeQuery(id+"F0.imprint","IMPRINT",EDGE,{"derivedFrom":sQuery(id+"F0.wireOp",EDGE,"E55.bottom")}),-1.0]])]});
            var Q2;
            Q2=makeQuery(id+"F0.imprint","IMPRINT",FACE,{"disambiguationData":[TD([[makeQuery(id+"F0.imprint","IMPRINT",EDGE,{"derivedFrom":sQuery(id+"F0.wireOp",EDGE,"E54.bottom")}),-1.0]])]});
            var Q3;
            Q3=makeQuery(id+"F0.imprint","IMPRINT",FACE,{"disambiguationData":[TD([[makeQuery(id+"F0.imprint","IMPRINT",EDGE,{"derivedFrom":sQuery(id+"F0.wireOp",EDGE,"E53.bottom")}),-1.0]])]});
            var Q4;
            Q4=makeQuery(id+"F0.imprint","IMPRINT",FACE,{"disambiguationData":[TD([[makeQuery(id+"F0.imprint","IMPRINT",EDGE,{"derivedFrom":sQuery(id+"F0.wireOp",EDGE,"E52.bottom")}),-1.0]])]});
            var Q5;
            Q5=makeQuery(id+"F0.imprint","IMPRINT",FACE,{"disambiguationData":[TD([[makeQuery(id+"F0.imprint","IMPRINT",EDGE,{"derivedFrom":sQuery(id+"F0.wireOp",EDGE,"E51.bottom")}),-1.0]])]});
            var Q6;
            Q6=makeQuery(id+"F0.imprint","IMPRINT",FACE,{"disambiguationData":[TD([[makeQuery(id+"F0.imprint","IMPRINT",EDGE,{"derivedFrom":sQuery(id+"F0.wireOp",EDGE,"E50.bottom")}),-1.0]])]});
            var Q7;
            Q7=makeQuery(id+"F0.imprint","IMPRINT",FACE,{"disambiguationData":[TD([[makeQuery(id+"F0.imprint","IMPRINT",EDGE,{"derivedFrom":sQuery(id+"F0.wireOp",EDGE,"E56.bottom")}),-1.0]])]});
            extrude(context, id + "F17", {"entities" : qUnion([Q0, Q1, Q2, Q3, Q4, Q5, Q6, Q7]), "operationType" : NewBodyOperationType.ADD, "depth" : 0.03 * mm});
        }
        {
            var Q0;
            {var subQ0=sQuery(id+"F0.wireOp",EDGE,"E24");Q0=makeQuery(id+"F0.imprint","IMPRINT",FACE,{"disambiguationData":[TD([[makeQuery(id+"F0.imprint","IMPRINT",EDGE,{"derivedFrom":subQ0}),-1.0]])]});}
            var Q1;
            {var subQ0=sQuery(id+"F0.wireOp",EDGE,"E23.left");Q1=makeQuery(id+"F0.imprint","IMPRINT",FACE,{"disambiguationData":[TD([[makeQuery(id+"F0.imprint","IMPRINT",EDGE,{"derivedFrom":subQ0}),-1.0]])]});}
            extrude(context, id + "F18", {"entities" : qUnion([Q0, Q1]), "operationType" : NewBodyOperationType.ADD, "depth" : 0.03 * mm});
        }
        {
            var Q0;
            Q0=makeQuery(id+"F0.imprint","IMPRINT",FACE,{"disambiguationData":[TD([[makeQuery(id+"F0.imprint","IMPRINT",EDGE,{"derivedFrom":sQuery(id+"F0.wireOp",EDGE,"E59.bottom")}),-1.0]])]});
            var Q1;
            Q1=makeQuery(id+"F0.imprint","IMPRINT",FACE,{"disambiguationData":[TD([[makeQuery(id+"F0.imprint","IMPRINT",EDGE,{"derivedFrom":sQuery(id+"F0.wireOp",EDGE,"E61.bottom")}),-1.0]])]});
            var Q2;
            Q2=makeQuery(id+"F0.imprint","IMPRINT",FACE,{"disambiguationData":[TD([[makeQuery(id+"F0.imprint","IMPRINT",EDGE,{"derivedFrom":sQuery(id+"F0.wireOp",EDGE,"E60.bottom")}),-1.0]])]});
            var Q3;
            Q3=makeQuery(id+"F0.imprint","IMPRINT",FACE,{"disambiguationData":[TD([[makeQuery(id+"F0.imprint","IMPRINT",EDGE,{"derivedFrom":sQuery(id+"F0.wireOp",EDGE,"E62.bottom")}),-1.0]])]});
            var Q4;
            Q4=makeQuery(id+"F0.imprint","IMPRINT",FACE,{"disambiguationData":[TD([[makeQuery(id+"F0.imprint","IMPRINT",EDGE,{"derivedFrom":sQuery(id+"F0.wireOp",EDGE,"E63.bottom")}),-1.0]])]});
            var Q5;
            Q5=makeQuery(id+"F0.imprint","IMPRINT",FACE,{"disambiguationData":[TD([[makeQuery(id+"F0.imprint","IMPRINT",EDGE,{"derivedFrom":sQuery(id+"F0.wireOp",EDGE,"E64.bottom")}),-1.0]])]});
            var Q6;
            Q6=makeQuery(id+"F0.imprint","IMPRINT",FACE,{"disambiguationData":[TD([[makeQuery(id+"F0.imprint","IMPRINT",EDGE,{"derivedFrom":sQuery(id+"F0.wireOp",EDGE,"E58.bottom")}),-1.0]])]});
            var Q7;
            Q7=makeQuery(id+"F0.imprint","IMPRINT",FACE,{"disambiguationData":[TD([[makeQuery(id+"F0.imprint","IMPRINT",EDGE,{"derivedFrom":sQuery(id+"F0.wireOp",EDGE,"E57.bottom")}),-1.0]])]});
            extrude(context, id + "F19", {"entities" : qUnion([Q0, Q1, Q2, Q3, Q4, Q5, Q6, Q7]), "operationType" : NewBodyOperationType.ADD, "depth" : 0.03 * mm});
        }
        {
            var Q0;
            Q0=makeQuery(id+"F0.imprint","IMPRINT",FACE,{"disambiguationData":[TD([[makeQuery(id+"F0.imprint","IMPRINT",EDGE,{"derivedFrom":sQuery(id+"F0.wireOp",EDGE,"E71")}),1.0]])]});
            var Q1;
            Q1=makeQuery(id+"F0.imprint","IMPRINT",FACE,{"disambiguationData":[TD([[makeQuery(id+"F0.imprint","IMPRINT",EDGE,{"derivedFrom":sQuery(id+"F0.wireOp",EDGE,"E70")}),1.0]])]});
            extrude(context, id + "F20", {"entities" : qUnion([Q0, Q1]), "operationType" : NewBodyOperationType.ADD, "depth" : 9.52 * mm});
        }
    });
